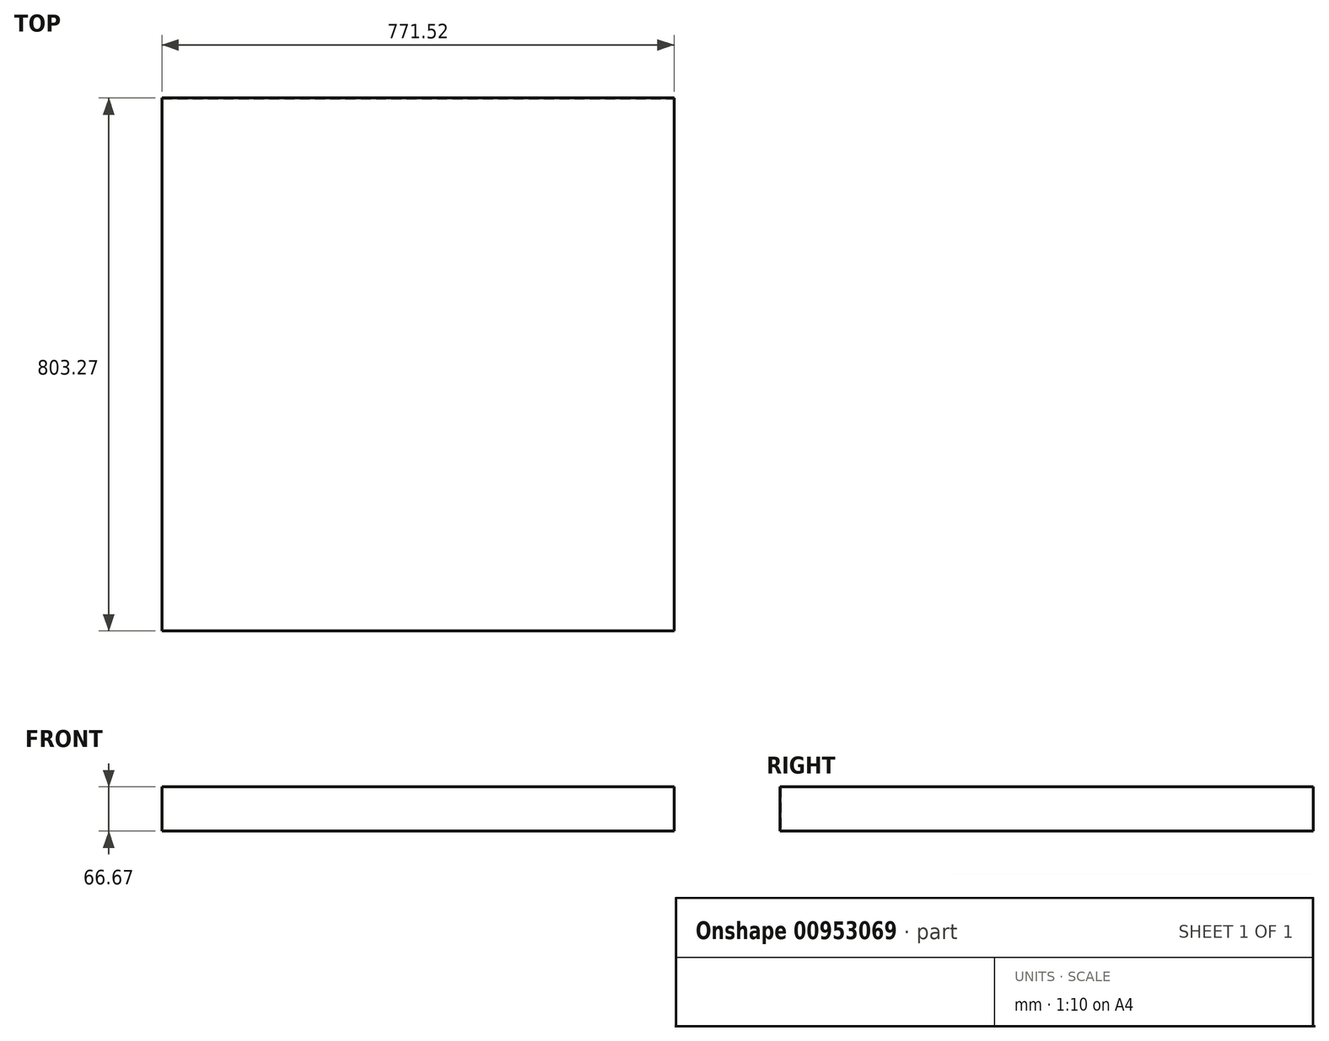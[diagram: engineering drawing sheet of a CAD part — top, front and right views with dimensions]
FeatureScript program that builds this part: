
annotation { "Feature Type Name" : "Feature", "Feature Type Description" : "" }
export const myFeature = defineFeature(function(context is Context, id is Id, definition is map)
    precondition{}
    {
        {
            var Q0;
            Q0=qCreatedBy(makeId("Top.planeOp"),FACE);
            var sketch = newSketch(context, id + "F0", { "sketchPlane" : qUnion([Q0])});
            skLineSegment(sketch, "E0", {"start": v(0, 0) * mm, "end": v(-771.53, 0) * mm});
            skLineSegment(sketch, "E1", {"start": v(-771.53, 0) * mm, "end": v(-771.53, 803.27) * mm});
            skLineSegment(sketch, "E2", {"start": v(-771.53, 803.27) * mm, "end": v(0, 803.27) * mm});
            skLineSegment(sketch, "E3", {"start": v(0, 803.27) * mm, "end": v(0, 0) * mm});
            skSolve(sketch);
        }
        {
            var Q0;
            Q0 = qSketchRegion(id + "F0", true);
            extrude(context, id + "F1", {"entities" : qUnion([Q0]), "depth" : 66.67 * mm, "offsetDistance" : 25.4 * mm});
        }
        {
            var Q0;
            Q0=makeQuery(id+"F1.opExtrude","CAP_FACE",FACE,{"disambiguationData":[OSD([sQuery(id+"F0.wireOp",EDGE,"E0"),sQuery(id+"F0.wireOp",EDGE,"E1"),sQuery(id+"F0.wireOp",EDGE,"E2"),sQuery(id+"F0.wireOp",EDGE,"E3")])],"isStart":true});
            shell(context, id + "F2", {"entities" : qUnion([Q0]), "thickness" : 0.81 * mm});
        }
    });
